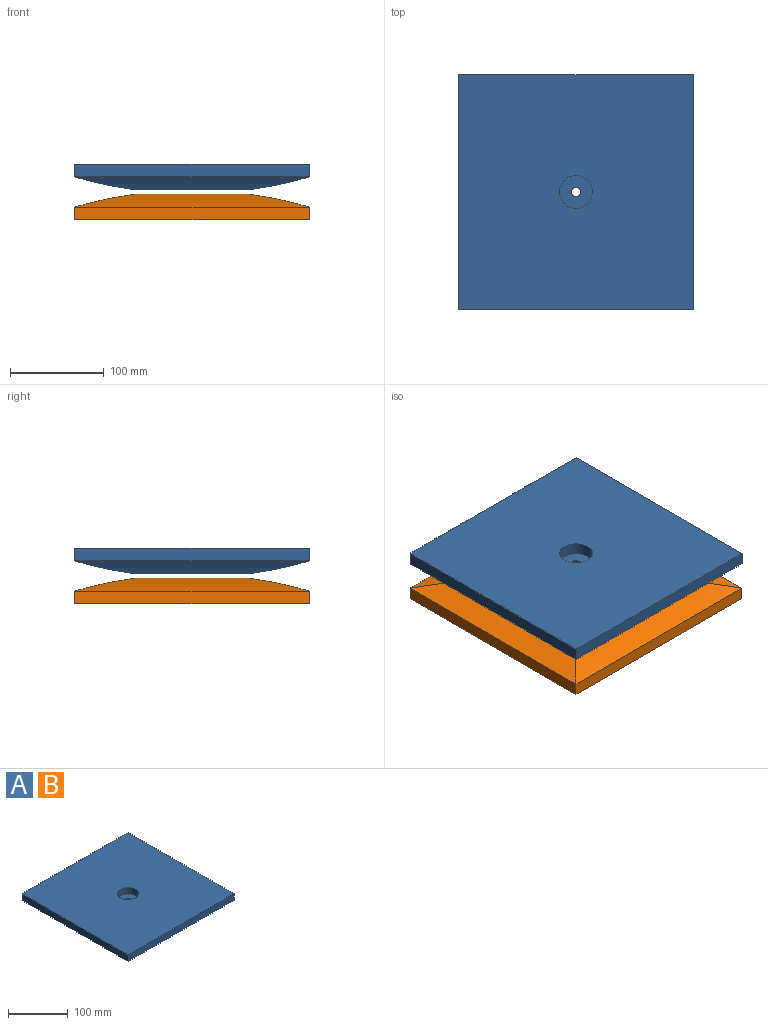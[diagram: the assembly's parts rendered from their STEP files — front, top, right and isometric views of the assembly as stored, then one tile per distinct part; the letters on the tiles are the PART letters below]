
ASSEMBLY  parts=2 mates=1
PART A: 13 faces, bbox 250x250x27 mm
  f0: plane 250x13.5mm, normal (0,1,0), area 3375mm2, adj f5,f6,f7,f12
  f1: plane 122.82x122.82mm, normal (0,0,-1), area 15005.1mm2, adj f3,f4,f10,f11,f12
  f2: plane 250x13.5mm, normal (0,-1,0), area 3375mm2, adj f5,f6,f7,f11
  f3: cylinder r=450mm len=250mm, axis (0,-1,0), area 12150mm2, adj f1,f6,f11,f12
  f4: cylinder r=450mm len=250mm, axis (0,-1,0), area 12150mm2, adj f1,f5,f11,f12
  f5: plane 250x13.5mm, normal (-1,0,0), area 3375mm2, adj f0,f2,f4,f7
  f6: plane 250x13.5mm, normal (1,0,0), area 3375mm2, adj f0,f2,f3,f7
  f7: plane 250x250mm, normal (0,0,1), area 61537.9mm2, adj f0,f2,f5,f6,f8
  f8: cylinder r=17.5mm len=35mm, axis (0,0,1), area 1429.4mm2, adj f7,f9
  f9: plane 35x35mm, normal (0,0,1), area 883.6mm2, adj f8,f10
  f10: cylinder r=5mm len=14mm, axis (0,0,1), area 439.8mm2, adj f1,f9
  f11: cylinder r=450mm len=250mm, axis (-1,0,0), area 12150mm2, adj f1,f2,f3,f4
  f12: cylinder r=450mm len=250mm, axis (-1,0,0), area 12150mm2, adj f0,f1,f3,f4
PART B: same geometry as A
PLACE A t=(-40.38,39.5,94.22)mm fixed
PLACE B rot(axis=(0,1,0),180deg) t=(209.62,39.5,89.22)mm
MATE revolute B.f8 <-> A.f8  axis (0,0,1) through (84.62,164.5,89.22)mm
